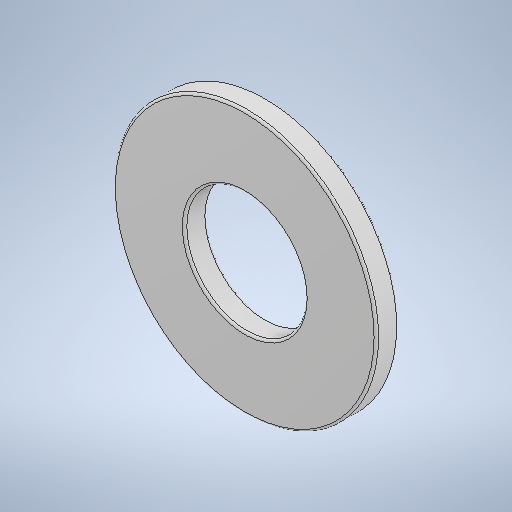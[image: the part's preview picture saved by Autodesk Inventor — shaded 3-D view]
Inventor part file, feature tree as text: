
AUTODESK INVENTOR PART (.ipt)
format: ipt  version: 2025 (Build 290162000, 162)  size: 259,072 bytes
history: native  units: in
note: dims shown in document units (in); Inventor stores cm internally (conversion verified against a paired STEP export)
features: fillet x1
ambient origin geometry x8: Origin, YZ Plane, XZ Plane, XY Plane, X Axis, Y Axis, Z Axis, Center Point
bodies: Solid1 (feature_tree)
feature tree (1):
  fillet  "Fillet1"  [1 undecoded]
note: 1 required parameter value undecoded (feature->parameter linkage not recoverable at this tier; creation-order binding heuristic only, values carry confidence <= 0.55)
